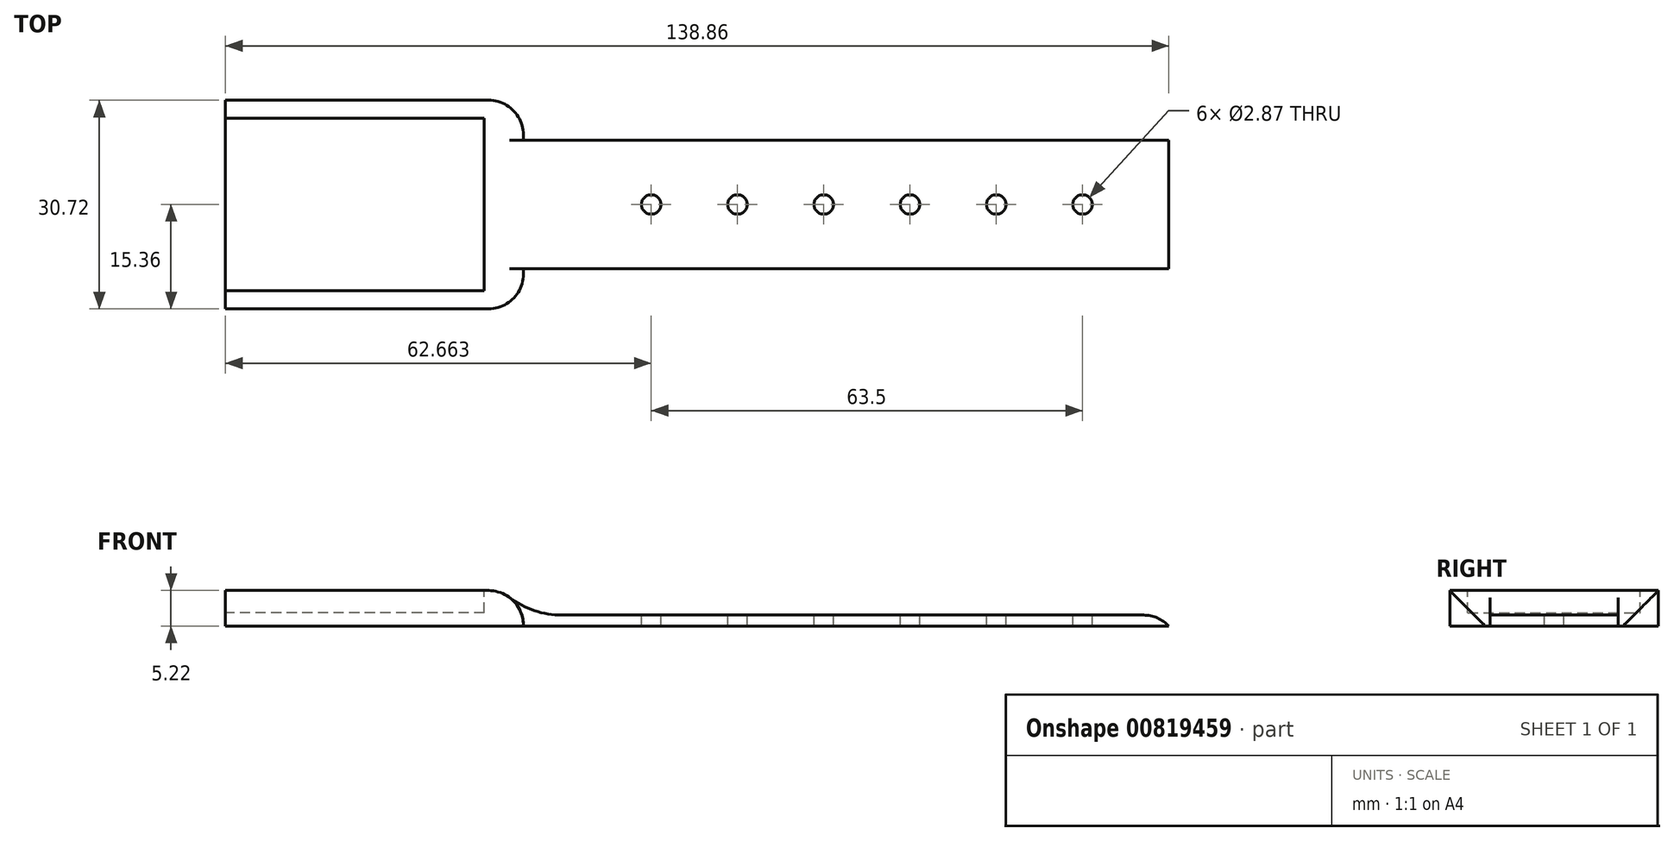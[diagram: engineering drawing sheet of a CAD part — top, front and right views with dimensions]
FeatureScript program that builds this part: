
annotation { "Feature Type Name" : "Feature", "Feature Type Description" : "" }
export const myFeature = defineFeature(function(context is Context, id is Id, definition is map)
    precondition{}
    {
        {
            var Q0;
            Q0=qCreatedBy(makeId("Top.planeOp"),FACE);
            var sketch = newSketch(context, id + "F0", { "sketchPlane" : qUnion([Q0])});
            skLineSegment(sketch, "E0.bottom", {"start": v(24.46, -15.36) * mm, "end": v(-24.46, -15.36) * mm});
            skLineSegment(sketch, "E0.top", {"start": v(24.46, 15.36) * mm, "end": v(-24.46, 15.36) * mm});
            skLineSegment(sketch, "E0.left", {"start": v(24.46, -15.36) * mm, "end": v(24.46, 15.36) * mm});
            skLineSegment(sketch, "E0.right", {"start": v(-24.46, -15.36) * mm, "end": v(-24.46, 15.36) * mm});
            skPoint(sketch, "E0.middle", {"position": v(0, 0) * mm});
            skLineSegment(sketch, "E1.bottom", {"start": v(-24.46, -9.45) * mm, "end": v(-119.48, -9.45) * mm});
            skLineSegment(sketch, "E1.top", {"start": v(-24.46, 9.45) * mm, "end": v(-119.48, 9.45) * mm});
            skLineSegment(sketch, "E1.left", {"start": v(-24.46, -9.45) * mm, "end": v(-24.46, 9.45) * mm});
            skLineSegment(sketch, "E1.right", {"start": v(-119.48, -9.45) * mm, "end": v(-119.48, 9.45) * mm});
            skLineSegment(sketch, "E2.MirrorCS", {"start": v(24.46, 9.45) * mm, "end": v(119.48, 9.45) * mm});
            skLineSegment(sketch, "E3.MirrorCS", {"start": v(119.48, -9.45) * mm, "end": v(119.48, 9.45) * mm});
            skLineSegment(sketch, "E4.MirrorCS", {"start": v(24.46, -9.45) * mm, "end": v(119.48, -9.45) * mm});
            skSolve(sketch);
        }
        {
            var Q0;
            Q0=qSketchRegion(id+"F0",true);
            extrude(context, id + "F1", {"entities" : qUnion([Q0]), "depth" : 1.6 * mm, "offsetDistance" : 25.4 * mm});
        }
        {
            var Q0;
            Q0=makeQuery(id+"F1.opExtrude","CAP_FACE",FACE,{"disambiguationData":[OSD([sQuery(id+"F0.wireOp",EDGE,"E0.bottom"),sQuery(id+"F0.wireOp",EDGE,"E0.top"),sQuery(id+"F0.wireOp",EDGE,"E0.left"),sQuery(id+"F0.wireOp",EDGE,"E0.right"),sQuery(id+"F0.wireOp",EDGE,"E1.bottom"),sQuery(id+"F0.wireOp",EDGE,"E1.top"),sQuery(id+"F0.wireOp",EDGE,"E1.right"),sQuery(id+"F0.wireOp",EDGE,"E2.MirrorCS"),sQuery(id+"F0.wireOp",EDGE,"E3.MirrorCS"),sQuery(id+"F0.wireOp",EDGE,"E4.MirrorCS")])],"isStart":false});
            var sketch = newSketch(context, id + "F2", { "sketchPlane" : qUnion([Q0])});
            skLineSegment(sketch, "E5", {"start": v(119.48, 0) * mm, "end": v(106.78, 0) * mm, "construction": true});
            skLineSegment(sketch, "E6", {"start": v(106.78, 0) * mm, "end": v(94.08, 0) * mm, "construction": true});
            skLineSegment(sketch, "E7", {"start": v(94.08, 0) * mm, "end": v(81.38, 0) * mm, "construction": true});
            skLineSegment(sketch, "E8", {"start": v(81.38, 0) * mm, "end": v(68.68, 0) * mm, "construction": true});
            skLineSegment(sketch, "E9", {"start": v(68.68, 0) * mm, "end": v(55.98, 0) * mm, "construction": true});
            skLineSegment(sketch, "E10", {"start": v(55.98, 0) * mm, "end": v(43.28, 0) * mm, "construction": true});
            skCircle(sketch, "E11", {"center": v(106.78, 0) * mm, "radius": 1.44 * mm});
            skCircle(sketch, "E12", {"center": v(94.08, 0) * mm, "radius": 1.44 * mm});
            skCircle(sketch, "E13", {"center": v(81.38, 0) * mm, "radius": 1.44 * mm});
            skCircle(sketch, "E14", {"center": v(68.68, 0) * mm, "radius": 1.44 * mm});
            skCircle(sketch, "E15", {"center": v(55.98, 0) * mm, "radius": 1.44 * mm});
            skCircle(sketch, "E16", {"center": v(43.28, 0) * mm, "radius": 1.44 * mm});
            skSolve(sketch);
        }
        {
            var Q0;
            Q0=qSketchRegion(id+"F2",true);
            extrude(context, id + "F3", {"entities" : qUnion([Q0]), "operationType" : NewBodyOperationType.REMOVE, "oppositeDirection" : true, "depth" : 25.4 * mm, "offsetDistance" : 25.4 * mm});
        }
        {
            var Q0;
            Q0=makeQuery(id+"F2.imprint","IMPRINT",FACE,{"disambiguationData":[TD([[makeQuery(id+"F2.imprint","IMPRINT",EDGE,{"derivedFrom":sQuery(id+"F2.wireOp",EDGE,"E11")}),-1.0]])]});
            var sketch = newSketch(context, id + "F4", { "sketchPlane" : qUnion([Q0])});
            skLineSegment(sketch, "E17", {"start": v(-119.47, 0) * mm, "end": v(-106.77, 0) * mm, "construction": true});
            skLineSegment(sketch, "E18", {"start": v(-106.77, 0) * mm, "end": v(-94.07, 0) * mm, "construction": true});
            skLineSegment(sketch, "E19", {"start": v(-94.07, 0) * mm, "end": v(-81.37, 0) * mm, "construction": true});
            skLineSegment(sketch, "E20", {"start": v(-81.37, 0) * mm, "end": v(-68.67, 0) * mm, "construction": true});
            skLineSegment(sketch, "E21", {"start": v(-68.67, 0) * mm, "end": v(-55.97, 0) * mm, "construction": true});
            skLineSegment(sketch, "E22", {"start": v(-55.97, 0) * mm, "end": v(-43.27, 0) * mm, "construction": true});
            skCircle(sketch, "E23", {"center": v(-106.77, 0) * mm, "radius": 1.4 * mm});
            skCircle(sketch, "E24", {"center": v(-94.07, 0) * mm, "radius": 1.4 * mm});
            skCircle(sketch, "E25", {"center": v(-81.37, 0) * mm, "radius": 1.4 * mm});
            skCircle(sketch, "E26", {"center": v(-68.67, 0) * mm, "radius": 1.4 * mm});
            skCircle(sketch, "E27", {"center": v(-55.97, 0) * mm, "radius": 1.4 * mm});
            skCircle(sketch, "E28", {"center": v(-43.27, 0) * mm, "radius": 1.4 * mm});
            skSolve(sketch);
        }
        {
            var Q0;
            Q0=qSketchRegion(id+"F4",true);
            extrude(context, id + "F5", {"entities" : qUnion([Q0]), "operationType" : NewBodyOperationType.ADD, "depth" : 2.54 * mm, "offsetDistance" : 25.4 * mm});
        }
        {
            var Q0;
            Q0=makeQuery(id+"F1.opExtrude","CAP_FACE",FACE,{"disambiguationData":[OSD([sQuery(id+"F0.wireOp",EDGE,"E0.bottom"),sQuery(id+"F0.wireOp",EDGE,"E0.top"),sQuery(id+"F0.wireOp",EDGE,"E0.left"),sQuery(id+"F0.wireOp",EDGE,"E0.right"),sQuery(id+"F0.wireOp",EDGE,"E1.bottom"),sQuery(id+"F0.wireOp",EDGE,"E1.top"),sQuery(id+"F0.wireOp",EDGE,"E1.right"),sQuery(id+"F0.wireOp",EDGE,"E2.MirrorCS"),sQuery(id+"F0.wireOp",EDGE,"E3.MirrorCS"),sQuery(id+"F0.wireOp",EDGE,"E4.MirrorCS")])],"isStart":false});
            var sketch = newSketch(context, id + "F6", { "sketchPlane" : qUnion([Q0])});
            skLineSegment(sketch, "E29.bottom", {"start": v(-24.46, 15.36) * mm, "end": v(24.46, 15.36) * mm});
            skLineSegment(sketch, "E29.top", {"start": v(-24.46, -15.36) * mm, "end": v(24.46, -15.36) * mm});
            skLineSegment(sketch, "E29.left", {"start": v(-24.46, 15.36) * mm, "end": v(-24.46, -15.36) * mm});
            skLineSegment(sketch, "E29.right", {"start": v(24.46, 15.36) * mm, "end": v(24.46, -15.36) * mm});
            skSolve(sketch);
        }
        {
            var Q0;
            Q0=qSketchRegion(id+"F6",true);
            extrude(context, id + "F7", {"entities" : qUnion([Q0]), "operationType" : NewBodyOperationType.ADD, "depth" : 3.62 * mm, "offsetDistance" : 25.4 * mm});
        }
        {
            var Q0;
            Q0=makeQuery(id+"F7.opExtrude","CAP_EDGE",EDGE,{"disambiguationData":[OSD([sQuery(id+"F6.wireOp",EDGE,"E29.right")])],"isStart":false});
            var Q1;
            Q1=makeQuery(id+"F7.opExtrude","CAP_EDGE",EDGE,{"disambiguationData":[OSD([sQuery(id+"F6.wireOp",EDGE,"E29.left")])],"isStart":false});
            var Q2;
            Q2=makeQuery(id+"F7.boolean.opBoolean","MERGE",EDGE,{"derivedFrom":[makeQuery(id+"F1.opExtrude","SWEPT_EDGE",EDGE,{"disambiguationData":[OSD([sQuery(id+"F0.wireOp",EDGE,"E0.top"),sQuery(id+"F0.wireOp",EDGE,"E0.right")])]}),makeQuery(id+"F7.opExtrude","SWEPT_EDGE",EDGE,{"disambiguationData":[OSD([sQuery(id+"F6.wireOp",EDGE,"E29.bottom"),sQuery(id+"F6.wireOp",EDGE,"E29.left")])]})]});
            var Q3;
            Q3=makeQuery(id+"F7.boolean.opBoolean","MERGE",EDGE,{"derivedFrom":[makeQuery(id+"F1.opExtrude","SWEPT_EDGE",EDGE,{"disambiguationData":[OSD([sQuery(id+"F0.wireOp",EDGE,"E0.bottom"),sQuery(id+"F0.wireOp",EDGE,"E0.right")])]}),makeQuery(id+"F7.opExtrude","SWEPT_EDGE",EDGE,{"disambiguationData":[OSD([sQuery(id+"F6.wireOp",EDGE,"E29.top"),sQuery(id+"F6.wireOp",EDGE,"E29.left")])]})]});
            var Q4;
            Q4=makeQuery(id+"F7.boolean.opBoolean","MERGE",EDGE,{"derivedFrom":[makeQuery(id+"F1.opExtrude","SWEPT_EDGE",EDGE,{"disambiguationData":[OSD([sQuery(id+"F0.wireOp",EDGE,"E0.bottom"),sQuery(id+"F0.wireOp",EDGE,"E0.left")])]}),makeQuery(id+"F7.opExtrude","SWEPT_EDGE",EDGE,{"disambiguationData":[OSD([sQuery(id+"F6.wireOp",EDGE,"E29.top"),sQuery(id+"F6.wireOp",EDGE,"E29.right")])]})]});
            var Q5;
            Q5=makeQuery(id+"F7.boolean.opBoolean","MERGE",EDGE,{"derivedFrom":[makeQuery(id+"F1.opExtrude","SWEPT_EDGE",EDGE,{"disambiguationData":[OSD([sQuery(id+"F0.wireOp",EDGE,"E0.top"),sQuery(id+"F0.wireOp",EDGE,"E0.left")])]}),makeQuery(id+"F7.opExtrude","SWEPT_EDGE",EDGE,{"disambiguationData":[OSD([sQuery(id+"F6.wireOp",EDGE,"E29.bottom"),sQuery(id+"F6.wireOp",EDGE,"E29.right")])]})]});
            fillet(context, id + "F8", {"entities" : qUnion([Q0, Q1, Q2, Q3, Q4, Q5]), "radius" : 5.08 * mm, "tangentPropagation" : true, "allowEdgeOverflow" : false});
        }
        {
            var Q0;
            Q0=makeQuery(id+"F1.opExtrude","CAP_EDGE",EDGE,{"disambiguationData":[OSD([sQuery(id+"F0.wireOp",EDGE,"E3.MirrorCS")])],"isStart":false});
            var Q1;
            Q1=makeQuery(id+"F1.opExtrude","CAP_EDGE",EDGE,{"disambiguationData":[OSD([sQuery(id+"F0.wireOp",EDGE,"E1.right")])],"isStart":false});
            fillet(context, id + "F9", {"entities" : qUnion([Q0, Q1]), "radius" : 5.08 * mm, "tangentPropagation" : true, "allowEdgeOverflow" : false});
        }
        {
            var Q0;
            {var subQ0=sQuery(id+"F0.wireOp",EDGE,"E4.MirrorCS");var subQ1=sQuery(id+"F0.wireOp",EDGE,"E0.left");var subQ2=sQuery(id+"F0.wireOp",EDGE,"E0.bottom");var subQ3=sQuery(id+"F0.wireOp",EDGE,"E0.top");var subQ4=sQuery(id+"F0.wireOp",EDGE,"E2.MirrorCS");var subQ5=sQuery(id+"F0.wireOp",EDGE,"E3.MirrorCS");var subQ6=sQuery(id+"F6.wireOp",EDGE,"E29.right");Q0=makeQuery(id+"F8.opFillet","BLEND_EDGE",EDGE,{"blendedFrom":[makeQuery(id+"F7.opExtrude","CAP_EDGE",EDGE,{"disambiguationData":[OSD([subQ6])],"isStart":false}),makeQuery(id+"F7.boolean.opBoolean","SPLIT",FACE,{"disambiguationData":[TD([makeQuery(id+"F1.opExtrude","SWEPT_FACE",FACE,{"disambiguationData":[OSD([subQ4])]})])],"derivedFrom":makeQuery(id+"F1.opExtrude","CAP_FACE",FACE,{"disambiguationData":[OSD([subQ2,subQ3,subQ1,sQuery(id+"F0.wireOp",EDGE,"E0.right"),sQuery(id+"F0.wireOp",EDGE,"E1.bottom"),sQuery(id+"F0.wireOp",EDGE,"E1.top"),sQuery(id+"F0.wireOp",EDGE,"E1.right"),subQ4,subQ5,subQ0])],"isStart":false})})],"blendedInto":[makeQuery(id+"F7.boolean.opBoolean","SPLIT",FACE,{"disambiguationData":[TD([makeQuery(id+"F1.opExtrude","SWEPT_FACE",FACE,{"disambiguationData":[OSD([subQ4])]})])],"derivedFrom":makeQuery(id+"F1.opExtrude","CAP_FACE",FACE,{"disambiguationData":[OSD([subQ2,subQ3,subQ1,sQuery(id+"F0.wireOp",EDGE,"E0.right"),sQuery(id+"F0.wireOp",EDGE,"E1.bottom"),sQuery(id+"F0.wireOp",EDGE,"E1.top"),sQuery(id+"F0.wireOp",EDGE,"E1.right"),subQ4,subQ5,subQ0])],"isStart":false})})]});}
            var Q1;
            {var subQ0=sQuery(id+"F0.wireOp",EDGE,"E1.right");var subQ1=sQuery(id+"F0.wireOp",EDGE,"E0.right");var subQ2=sQuery(id+"F0.wireOp",EDGE,"E0.bottom");var subQ4=sQuery(id+"F0.wireOp",EDGE,"E1.bottom");var subQ5=sQuery(id+"F0.wireOp",EDGE,"E0.top");var subQ6=sQuery(id+"F0.wireOp",EDGE,"E1.top");var subQ7=sQuery(id+"F6.wireOp",EDGE,"E29.left");Q1=makeQuery(id+"F8.opFillet","BLEND_EDGE",EDGE,{"blendedFrom":[makeQuery(id+"F7.opExtrude","CAP_EDGE",EDGE,{"disambiguationData":[OSD([subQ7])],"isStart":false}),makeQuery(id+"F7.boolean.opBoolean","SPLIT",FACE,{"disambiguationData":[TD([makeQuery(id+"F1.opExtrude","SWEPT_FACE",FACE,{"disambiguationData":[OSD([subQ4])]})])],"derivedFrom":makeQuery(id+"F1.opExtrude","CAP_FACE",FACE,{"disambiguationData":[OSD([subQ2,subQ5,sQuery(id+"F0.wireOp",EDGE,"E0.left"),subQ1,subQ4,subQ6,subQ0,sQuery(id+"F0.wireOp",EDGE,"E2.MirrorCS"),sQuery(id+"F0.wireOp",EDGE,"E3.MirrorCS"),sQuery(id+"F0.wireOp",EDGE,"E4.MirrorCS")])],"isStart":false})})],"blendedInto":[makeQuery(id+"F7.boolean.opBoolean","SPLIT",FACE,{"disambiguationData":[TD([makeQuery(id+"F1.opExtrude","SWEPT_FACE",FACE,{"disambiguationData":[OSD([subQ4])]})])],"derivedFrom":makeQuery(id+"F1.opExtrude","CAP_FACE",FACE,{"disambiguationData":[OSD([subQ2,subQ5,sQuery(id+"F0.wireOp",EDGE,"E0.left"),subQ1,subQ4,subQ6,subQ0,sQuery(id+"F0.wireOp",EDGE,"E2.MirrorCS"),sQuery(id+"F0.wireOp",EDGE,"E3.MirrorCS"),sQuery(id+"F0.wireOp",EDGE,"E4.MirrorCS")])],"isStart":false})})]});}
            fillet(context, id + "F10", {"entities" : qUnion([Q0, Q1]), "radius" : 12.7 * mm, "tangentPropagation" : true, "allowEdgeOverflow" : false});
        }
        {
            var Q0;
            Q0=qCreatedBy(makeId("Right.planeOp"),FACE);
            cPlane(context, id + "F11", {"entities" : qUnion([Q0]), "cplaneType" : CPlaneType.OFFSET, "offset" : 19.38 * mm, "oppositeDirection" : true, "width" : 152.4 * mm, "height" : 152.4 * mm});
        }
        {
            var Q0;
            Q0=qCreatedBy(id+"F11.planeOp",FACE);
            var sketch = newSketch(context, id + "F12", { "sketchPlane" : qUnion([Q0])});
            skCircle(sketch, "E30", {"center": v(0, 0) * mm, "radius": 33.13 * mm});
            skSolve(sketch);
        }
        {
            var Q0;
            Q0 = qSketchRegion(id + "F12", true);
            extrude(context, id + "F13", {"entities" : qUnion([Q0]), "operationType" : NewBodyOperationType.REMOVE, "oppositeDirection" : true, "depth" : 102.87 * mm, "offsetDistance" : 25.4 * mm});
        }
        {
            var Q0;
            Q0=qCreatedBy(id+"F11.planeOp",FACE);
            var sketch = newSketch(context, id + "F14", { "sketchPlane" : qUnion([Q0])});
            skLineSegment(sketch, "E31", {"start": v(0, 0) * mm, "end": v(0, 4) * mm, "construction": true});
            skLineSegment(sketch, "E32.bottom", {"start": v(-12.7, 1.97) * mm, "end": v(12.7, 1.97) * mm});
            skLineSegment(sketch, "E32.top", {"start": v(-12.7, 6.03) * mm, "end": v(12.7, 6.03) * mm});
            skLineSegment(sketch, "E32.left", {"start": v(-12.7, 1.97) * mm, "end": v(-12.7, 6.03) * mm});
            skLineSegment(sketch, "E32.right", {"start": v(12.7, 1.97) * mm, "end": v(12.7, 6.03) * mm});
            skPoint(sketch, "E32.middle", {"position": v(0, 4) * mm});
            skSolve(sketch);
        }
        {
            var Q0;
            Q0 = qSketchRegion(id + "F14", true);
            extrude(context, id + "F15", {"entities" : qUnion([Q0]), "operationType" : NewBodyOperationType.REMOVE, "depth" : 38.1 * mm, "offsetDistance" : 25.4 * mm});
        }
    });
